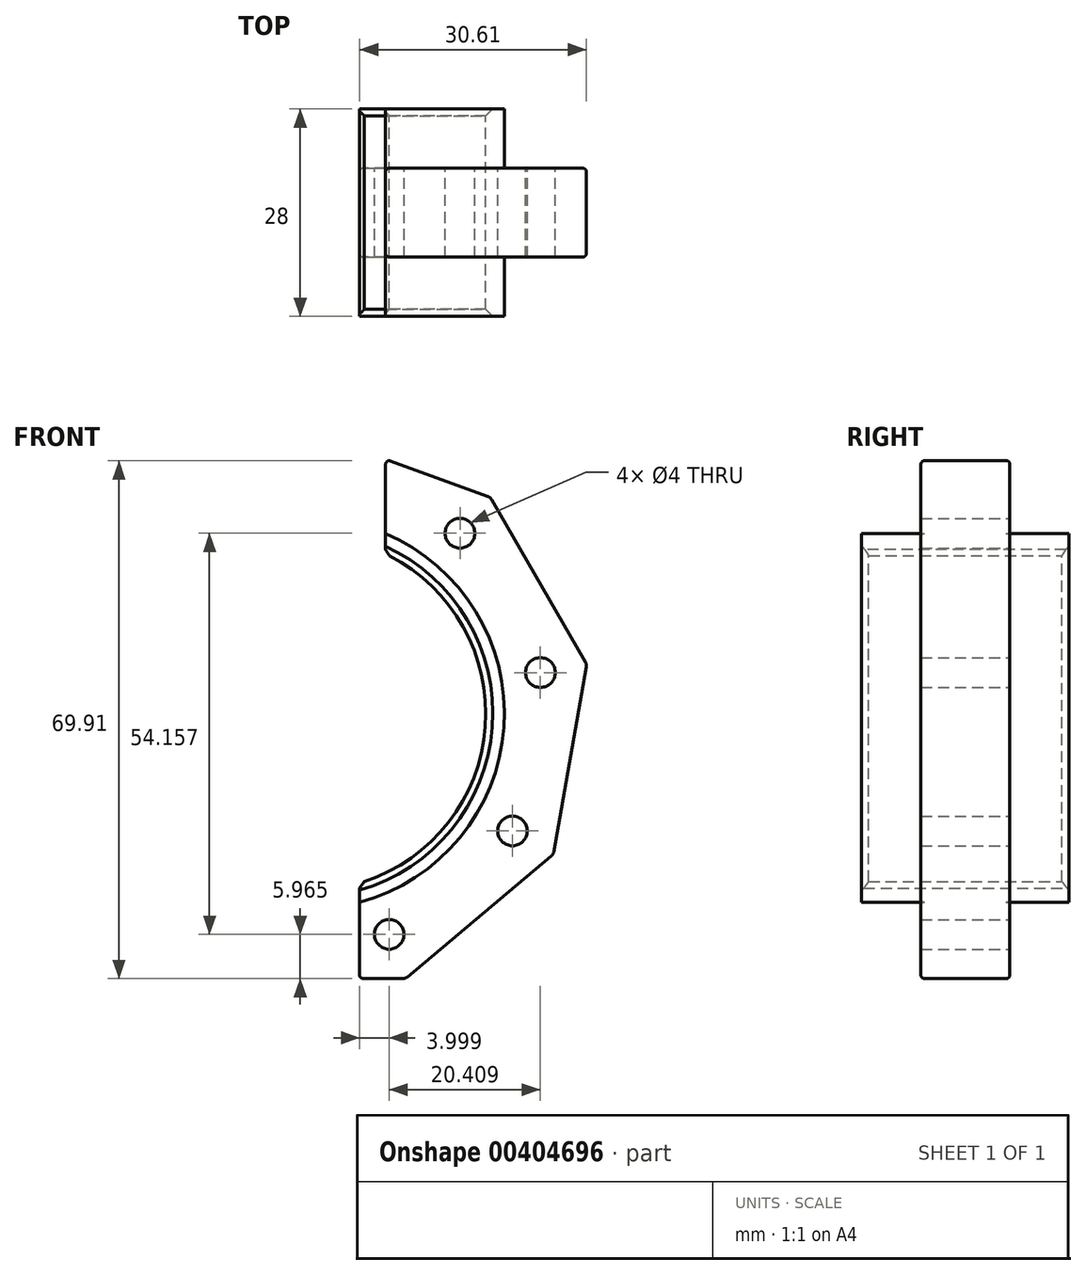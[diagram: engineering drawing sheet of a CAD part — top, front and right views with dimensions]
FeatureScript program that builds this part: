
annotation { "Feature Type Name" : "Feature", "Feature Type Description" : "" }
export const myFeature = defineFeature(function(context is Context, id is Id, definition is map)
    precondition{}
    {
        {
            var Q0;
            Q0=qCreatedBy(makeId("Front.planeOp"),FACE);
            var sketch = newSketch(context, id + "F0", { "sketchPlane" : qUnion([Q0])});
            skArc(sketch, "E0", {"start": v(6.86, -24.46) * mm, "mid": v(25.33, -1.86) * mm, "end": v(10.36, 23.2) * mm});
            skLineSegment(sketch, "E1.0", {"start": v(10.36, 34.33) * mm, "end": v(24.5, 29.19) * mm});
            skLineSegment(sketch, "E1.1", {"start": v(24.5, 29.19) * mm, "end": v(37.52, 6.62) * mm});
            skLineSegment(sketch, "E1.2", {"start": v(37.52, 6.62) * mm, "end": v(33, -19.05) * mm});
            skLineSegment(sketch, "E1.3", {"start": v(33, -19.05) * mm, "end": v(13.03, -35.8) * mm});
            skLineSegment(sketch, "E1.4", {"start": v(13.03, -35.8) * mm, "end": v(6.86, -35.8) * mm});
            skCircle(sketch, "E2.0", {"center": v(20.4, 24.32) * mm, "radius": 2 * mm});
            skPoint(sketch, "E3.0", {"position": v(33, -19.05) * mm});
            skCircle(sketch, "E4", {"center": v(27.5, -15.88) * mm, "radius": 2 * mm});
            skPoint(sketch, "E5.0", {"position": v(37.52, 6.62) * mm});
            skCircle(sketch, "E6", {"center": v(31.27, 5.51) * mm, "radius": 2 * mm});
            skPoint(sketch, "E7.0", {"position": v(13.03, -35.8) * mm});
            skCircle(sketch, "E8", {"center": v(10.86, -29.84) * mm, "radius": 2 * mm});
            skLineSegment(sketch, "E9", {"start": v(8.86, -29.84) * mm, "end": v(6.86, -29.84) * mm, "construction": true});
            skLineSegment(sketch, "E10", {"start": v(6.86, -24.46) * mm, "end": v(6.86, -35.8) * mm});
            skLineSegment(sketch, "E11", {"start": v(10.36, 23.2) * mm, "end": v(10.36, 34.33) * mm});
            skPoint(sketch, "E12.0.start.orphan", {"position": v(6.86, -22.37) * mm});
            skPoint(sketch, "E13.orphan", {"position": v(10.36, 20.98) * mm});
            skArc(sketch, "E14", {"start": v(0, 26.4) * mm, "mid": v(26.4, 0) * mm, "end": v(0, -26.4) * mm});
            skArc(sketch, "E15", {"start": v(0, 23.9) * mm, "mid": v(23.9, 0) * mm, "end": v(0, -23.9) * mm});
            skPoint(sketch, "E16.orphan", {"position": v(10.36, 22.09) * mm});
            skPoint(sketch, "E17.start.orphan", {"position": v(6.86, -26.53) * mm});
            skLineSegment(sketch, "E18", {"start": v(10.36, 23.2) * mm, "end": v(10.36, 21.54) * mm});
            skLineSegment(sketch, "E19", {"start": v(6.86, -24.46) * mm, "end": v(6.86, -22.9) * mm});
            skSolve(sketch);
        }
        {
            var Q0;
            {var subQ2=sQuery(id+"F0.wireOp",EDGE,"E1.0");Q0=makeQuery(id+"F0.imprint","IMPRINT",FACE,{"disambiguationData":[TD([[makeQuery(id+"F0.imprint","IMPRINT",EDGE,{"derivedFrom":subQ2}),-1.0]])]});}
            var Q1;
            {var subQ0=sQuery(id+"F0.wireOp",EDGE,"E0");Q1=makeQuery(id+"F0.imprint","IMPRINT",FACE,{"disambiguationData":[TD([[makeQuery(id+"F0.imprint","IMPRINT",EDGE,{"derivedFrom":subQ0}),-1.0]])]});}
            extrude(context, id + "F1", {"entities" : qUnion([Q0, Q1]), "depth" : 12 * mm, "symmetric" : true});
        }
        {
            var Q0;
            Q0=makeQuery(id+"F0.imprint","IMPRINT",FACE,{"disambiguationData":[TD([[makeQuery(id+"F0.imprint","IMPRINT",EDGE,{"derivedFrom":sQuery(id+"F0.wireOp",EDGE,"E0")}),1.0]])]});
            var Q1;
            {var subQ0=sQuery(id+"F0.wireOp",EDGE,"E0");Q1=makeQuery(id+"F0.imprint","IMPRINT",FACE,{"disambiguationData":[TD([[makeQuery(id+"F0.imprint","IMPRINT",EDGE,{"derivedFrom":subQ0}),-1.0]])]});}
            extrude(context, id + "F2", {"entities" : qUnion([Q0, Q1]), "operationType" : NewBodyOperationType.ADD, "depth" : 28 * mm, "symmetric" : true});
        }
        {
            var Q0;
            Q0=makeQuery(id+"F2.opExtrude","SWEPT_EDGE",EDGE,{"disambiguationData":[OSD([sQuery(id+"F0.wireOp",EDGE,"E15"),sQuery(id+"F0.wireOp",EDGE,"E18")])]});
            var Q1;
            Q1=makeQuery(id+"F2.opExtrude","CAP_EDGE",EDGE,{"disambiguationData":[OSD([sQuery(id+"F0.wireOp",EDGE,"E15")])],"isStart":false});
            var Q2;
            Q2=makeQuery(id+"F2.opExtrude","CAP_EDGE",EDGE,{"disambiguationData":[OSD([sQuery(id+"F0.wireOp",EDGE,"E15")])],"isStart":true});
            var Q3;
            Q3=makeQuery(id+"F2.opExtrude","SWEPT_EDGE",EDGE,{"disambiguationData":[OSD([sQuery(id+"F0.wireOp",EDGE,"E15"),sQuery(id+"F0.wireOp",EDGE,"E19")])]});
            chamfer(context, id + "F3", {"entities" : qUnion([Q0, Q1, Q2, Q3]), "width" : .945 * mm, "tangentPropagation" : true});
        }
        {
            var Q0;
            Q0=makeQuery(id+"F1.opExtrude","SWEPT_EDGE",EDGE,{"disambiguationData":[OSD([sQuery(id+"F0.wireOp",EDGE,"E1.0"),sQuery(id+"F0.wireOp",EDGE,"E1.1")])]});
            var Q1;
            Q1=makeQuery(id+"F1.opExtrude","SWEPT_EDGE",EDGE,{"disambiguationData":[OSD([sQuery(id+"F0.wireOp",EDGE,"E1.1"),sQuery(id+"F0.wireOp",EDGE,"E1.2")])]});
            var Q2;
            Q2=makeQuery(id+"F1.opExtrude","SWEPT_EDGE",EDGE,{"disambiguationData":[OSD([sQuery(id+"F0.wireOp",EDGE,"E1.2"),sQuery(id+"F0.wireOp",EDGE,"E1.3")])]});
            var Q3;
            Q3=makeQuery(id+"F1.opExtrude","SWEPT_EDGE",EDGE,{"disambiguationData":[OSD([sQuery(id+"F0.wireOp",EDGE,"E1.3"),sQuery(id+"F0.wireOp",EDGE,"E1.4")])]});
            fillet(context, id + "F4", {"entities" : qUnion([Q0, Q1, Q2, Q3]), "radius" : 1 * mm, "tangentPropagation" : true, "allowEdgeOverflow" : false});
        }
        {
            var Q0;
            Q0=makeQuery(id+"F1.opExtrude","CAP_EDGE",EDGE,{"disambiguationData":[OSD([sQuery(id+"F0.wireOp",EDGE,"E1.0")])],"isStart":false});
            var Q1;
            Q1=makeQuery(id+"F1.opExtrude","CAP_EDGE",EDGE,{"disambiguationData":[OSD([sQuery(id+"F0.wireOp",EDGE,"E1.1")])],"isStart":false});
            var Q2;
            Q2=makeQuery(id+"F1.opExtrude","CAP_EDGE",EDGE,{"disambiguationData":[OSD([sQuery(id+"F0.wireOp",EDGE,"E1.2")])],"isStart":false});
            var Q3;
            Q3=makeQuery(id+"F1.opExtrude","CAP_EDGE",EDGE,{"disambiguationData":[OSD([sQuery(id+"F0.wireOp",EDGE,"E1.3")])],"isStart":false});
            var Q4;
            Q4=makeQuery(id+"F1.opExtrude","CAP_EDGE",EDGE,{"disambiguationData":[OSD([sQuery(id+"F0.wireOp",EDGE,"E1.4")])],"isStart":false});
            var Q5;
            Q5=makeQuery(id+"F1.opExtrude","CAP_EDGE",EDGE,{"disambiguationData":[OSD([sQuery(id+"F0.wireOp",EDGE,"E10")])],"isStart":false});
            var Q6;
            Q6=makeQuery(id+"F1.opExtrude","CAP_EDGE",EDGE,{"disambiguationData":[OSD([sQuery(id+"F0.wireOp",EDGE,"E10")])],"isStart":true});
            var Q7;
            Q7=makeQuery(id+"F1.opExtrude","CAP_EDGE",EDGE,{"disambiguationData":[OSD([sQuery(id+"F0.wireOp",EDGE,"E1.4")])],"isStart":true});
            var Q8;
            Q8=makeQuery(id+"F1.opExtrude","CAP_EDGE",EDGE,{"disambiguationData":[OSD([sQuery(id+"F0.wireOp",EDGE,"E1.3")])],"isStart":true});
            var Q9;
            Q9=makeQuery(id+"F1.opExtrude","CAP_EDGE",EDGE,{"disambiguationData":[OSD([sQuery(id+"F0.wireOp",EDGE,"E1.2")])],"isStart":true});
            var Q10;
            Q10=makeQuery(id+"F1.opExtrude","CAP_EDGE",EDGE,{"disambiguationData":[OSD([sQuery(id+"F0.wireOp",EDGE,"E1.1")])],"isStart":true});
            var Q11;
            Q11=makeQuery(id+"F1.opExtrude","CAP_EDGE",EDGE,{"disambiguationData":[OSD([sQuery(id+"F0.wireOp",EDGE,"E1.0")])],"isStart":true});
            var Q12;
            Q12=makeQuery(id+"F1.opExtrude","SWEPT_EDGE",EDGE,{"disambiguationData":[OSD([sQuery(id+"F0.wireOp",EDGE,"E1.4"),sQuery(id+"F0.wireOp",EDGE,"E10")])]});
            var Q13;
            Q13=makeQuery(id+"F1.opExtrude","SWEPT_EDGE",EDGE,{"disambiguationData":[OSD([sQuery(id+"F0.wireOp",EDGE,"E1.0"),sQuery(id+"F0.wireOp",EDGE,"E11")])]});
            var Q14;
            Q14=makeQuery(id+"F1.opExtrude","CAP_EDGE",EDGE,{"disambiguationData":[OSD([sQuery(id+"F0.wireOp",EDGE,"E11")])],"isStart":false});
            var Q15;
            Q15=makeQuery(id+"F1.opExtrude","CAP_EDGE",EDGE,{"disambiguationData":[OSD([sQuery(id+"F0.wireOp",EDGE,"E11")])],"isStart":true});
            fillet(context, id + "F5", {"entities" : qUnion([Q0, Q1, Q2, Q3, Q4, Q5, Q6, Q7, Q8, Q9, Q10, Q11, Q12, Q13, Q14, Q15]), "radius" : .5 * mm, "allowEdgeOverflow" : false});
        }
    });
